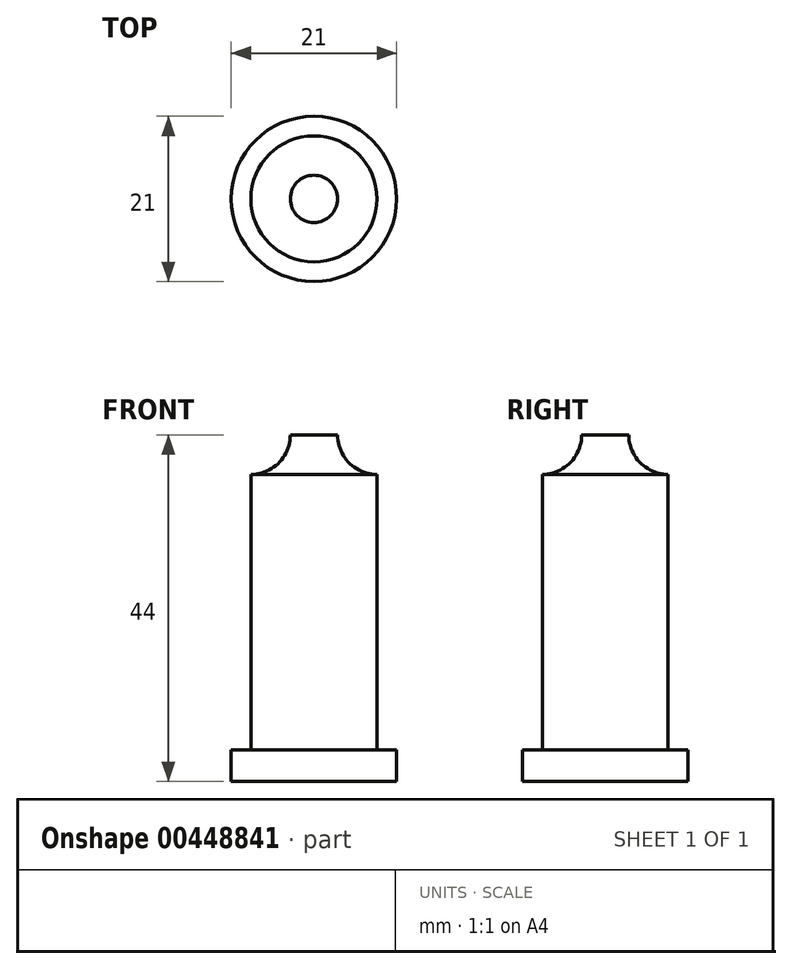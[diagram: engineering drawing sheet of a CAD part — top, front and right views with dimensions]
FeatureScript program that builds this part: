
annotation { "Feature Type Name" : "Feature", "Feature Type Description" : "" }
export const myFeature = defineFeature(function(context is Context, id is Id, definition is map)
    precondition{}
    {
        {
            var Q0;
            Q0=qCreatedBy(makeId("Top.planeOp"),FACE);
            var sketch = newSketch(context, id + "F0", { "sketchPlane" : qUnion([Q0])});
            skCircle(sketch, "E0", {"center": v(0, 0) * mm, "radius": 10.5 * mm});
            skSolve(sketch);
        }
        {
            var Q0;
            Q0=qSketchRegion(id+"F0",true);
            extrude(context, id + "F1", {"entities" : qUnion([Q0]), "depth" : 4 * mm});
        }
        {
            var Q0;
            Q0=qCreatedBy(makeId("Top.planeOp"),FACE);
            var sketch = newSketch(context, id + "F2", { "sketchPlane" : qUnion([Q0])});
            skCircle(sketch, "E1", {"center": v(0, 0) * mm, "radius": 8 * mm});
            skSolve(sketch);
        }
        {
            var Q0;
            Q0=qSketchRegion(id+"F2",true);
            extrude(context, id + "F3", {"entities" : qUnion([Q0]), "operationType" : NewBodyOperationType.ADD, "depth" : 39 * mm});
        }
        {
            var Q0;
            Q0=qCreatedBy(makeId("Right.planeOp"),FACE);
            var sketch = newSketch(context, id + "F4", { "sketchPlane" : qUnion([Q0])});
            skLineSegment(sketch, "E2", {"start": v(0, 44) * mm, "end": v(0, 39) * mm});
            skLineSegment(sketch, "E3", {"start": v(0, 39) * mm, "end": v(8, 39) * mm});
            skLineSegment(sketch, "E4", {"start": v(3, 44) * mm, "end": v(0, 44) * mm});
            skArc(sketch, "E5", {"start": v(3, 44) * mm, "mid": v(4.46, 40.46) * mm, "end": v(8, 39) * mm});
            skSolve(sketch);
        }
        {
            var Q0;
            Q0=makeQuery(id+"F4.imprint","IMPRINT",FACE,{"disambiguationData":[TD([[makeQuery(id+"F4.imprint","IMPRINT",EDGE,{"derivedFrom":sQuery(id+"F4.wireOp",EDGE,"E2")}),1.0]])]});
            var Q1;
            Q1=sQuery(id+"F4.wireOp",EDGE,"E2");
            revolve(context, id + "F5", {"operationType" : NewBodyOperationType.ADD, "entities" : qUnion([Q0]), "axis" : qUnion([Q1]), "revolveType" : RevolveType.FULL});
        }
    });
